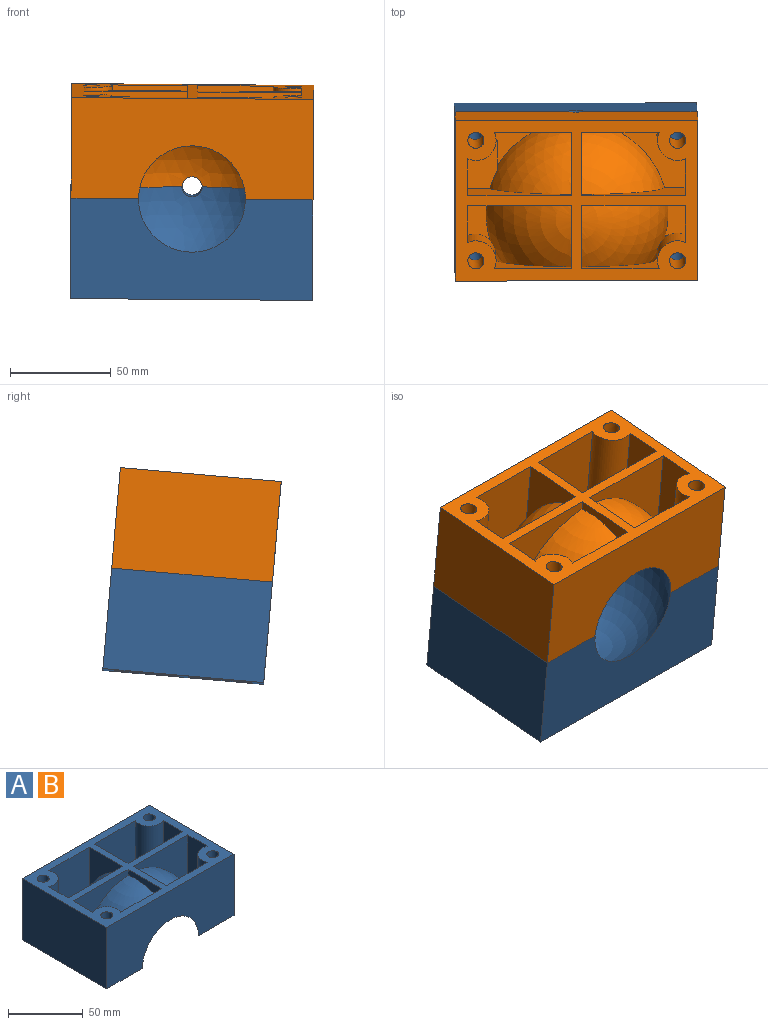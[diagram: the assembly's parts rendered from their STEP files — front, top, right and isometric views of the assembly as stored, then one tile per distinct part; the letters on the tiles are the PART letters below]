
ASSEMBLY  parts=2 mates=1
PART A: 56 faces, bbox 120x95.4x54 mm
  f0: sphere r=46mm, area 1832.9mm2, adj f1,f2,f8,f35,f38,f55
  f1: plane 44x38.34mm, normal (0,1,0), area 794.8mm2, adj f0,f17,f35,f38,f55
  f2: plane 51.5x39mm, normal (0,-1,0), area 971mm2, adj f0,f6,f8,f17,f55
  f3: plane 44x38.35mm, normal (0,-1,0), area 1642mm2, adj f4,f17,f37,f41,f53
  f4: sphere r=46mm, area 1825.4mm2, adj f3,f5,f34,f41,f49,f53
  f5: plane 51.5x39mm, normal (0,1,0), area 1034.3mm2, adj f4,f17,f34,f36,f53
  f6: plane 39x18.34mm, normal (1,0,0), area 715.1mm2, adj f2,f8,f17,f35
  f7: plane 44x18.34mm, normal (-1,0,0), area 806.7mm2, adj f9,f17,f46,f50
  f8: plane 20.7x11.33mm, normal (0,0,1), area 175.6mm2, adj f0,f2,f6,f35
  f9: plane 19.5x10mm, normal (0,0,1), area 156.5mm2, adj f7,f10,f46,f50
  f10: sphere r=46mm, area 1935.8mm2, adj f9,f40,f43,f46,f50,f54
  f11: plane 80x55mm, normal (0,0,-1), area 1917mm2, adj f13,f15,f16,f18,f19,f22,f23,f24
  f12: plane 80x55mm, normal (0,0,-1), area 1917mm2, adj f13,f14,f15,f18,f20,f21,f28,f29
  f13: plane 120x50mm, normal (0,1,0), area 5960.7mm2, adj f11,f12,f14,f16,f17,f33
  f14: plane 80x50mm, normal (-1,0,0), area 4000mm2, adj f12,f13,f15,f17
  f15: plane 120x50mm, normal (0,-1,0), area 4900.4mm2, adj f11,f12,f14,f16,f17,f18
  f16: plane 80x50mm, normal (1,0,0), area 4000mm2, adj f11,f13,f15,f17
  f17: plane 120x80mm, normal (0,0,1), area 3599.3mm2, adj f1,f2,f3,f5,f6,f7,f13,f14
  f18: sphere r=40mm, area 8757mm2, adj f11,f12,f15,f33
  f19: cylinder r=4mm len=50mm, axis (0,0,-1), area 1256.6mm2, adj f11,f17
  f20: cylinder r=4mm len=50mm, axis (0,0,-1), area 1256.6mm2, adj f12,f17
  f21: cylinder r=4mm len=50mm, axis (0,0,-1), area 1256.6mm2, adj f12,f17
  f22: cylinder r=4mm len=50mm, axis (0,0,-1), area 1256.6mm2, adj f11,f17
  f23: plane 10x4mm, normal (0,-1,0), area 40mm2, adj f11,f24,f26,f27
  f24: plane 40x4mm, normal (-1,0,0), area 160mm2, adj f11,f23,f25,f27
  f25: plane 10x4mm, normal (0,1,0), area 40mm2, adj f11,f24,f26,f27
  f26: plane 40x4mm, normal (1,0,0), area 160mm2, adj f11,f23,f25,f27
  f27: plane 40x10mm, normal (0,0,-1), area 400mm2, adj f23,f24,f25,f26
  f28: plane 10x5mm, normal (0,1,0), area 50mm2, adj f12,f29,f31,f32
  f29: plane 40x5mm, normal (1,0,0), area 200mm2, adj f12,f28,f30,f32
  f30: plane 10x5mm, normal (0,-1,0), area 50mm2, adj f12,f29,f31,f32
  f31: plane 40x5mm, normal (-1,0,0), area 200mm2, adj f12,f28,f30,f32
  f32: plane 40x10mm, normal (0,0,-1), area 400mm2, adj f28,f29,f30,f31
  f33: cylinder r=5mm len=10.31mm, axis (0,1,0), area 162mm2, adj f11,f12,f13,f18
  f34: plane 23.5x15mm, normal (0,0,1), area 270.1mm2, adj f4,f5,f36,f37,f48,f49
  f35: cylinder r=10mm len=44mm, axis (0,0,-1), area 935.1mm2, adj f0,f1,f6,f8,f17,f38
  f36: plane 39x18.33mm, normal (1,0,0), area 714.8mm2, adj f5,f17,f34,f37
  f37: cylinder r=10mm len=44mm, axis (0,0,-1), area 974.2mm2, adj f3,f17,f34,f36,f41,f48
  f38: plane 2.35x2.05mm, normal (0,0,1), area 2.2mm2, adj f0,f1,f35
  f39: plane 42x31.5mm, normal (0,0,1), area 470.6mm2, adj f42,f44,f45,f47,f51
  f40: plane 2.35x2.05mm, normal (0,0,1), area 2.2mm2, adj f10,f43,f46
  f41: plane 28.85x20.36mm, normal (0,0,1), area 211.3mm2, adj f3,f4,f37,f48,f49
  f42: plane 44x38.32mm, normal (0,-1,0), area 1640.9mm2, adj f17,f39,f45,f47,f52
  f43: plane 44x38.34mm, normal (0,1,0), area 794.8mm2, adj f10,f17,f40,f46,f54
  f44: plane 44x18.34mm, normal (-1,0,0), area 807mm2, adj f17,f39,f47,f51
  f45: sphere r=46mm, area 1882.6mm2, adj f39,f42,f51,f52
  f46: cylinder r=10mm len=44mm, axis (0,0,-1), area 991.7mm2, adj f7,f9,f10,f17,f40,f43
  f47: cylinder r=10mm len=44mm, axis (0,0,-1), area 1053.9mm2, adj f17,f39,f42,f44
  f48: plane 5x1.85mm, normal (0,1,0), area 9.2mm2, adj f34,f37,f41,f49
  f49: plane 14.23x5mm, normal (1,0,0), area 65.9mm2, adj f4,f34,f41,f48
  f50: plane 51.5x44mm, normal (0,-1,0), area 1018.2mm2, adj f7,f9,f10,f17,f54
  f51: plane 51.5x44mm, normal (0,1,0), area 1087.2mm2, adj f17,f39,f44,f45,f52
  f52: plane 36.82x31.5mm, normal (1,0,0), area 502mm2, adj f17,f42,f45,f51
  f53: plane 36.82x31.5mm, normal (-1,0,0), area 502mm2, adj f3,f4,f5,f17
  f54: plane 31.5x10.84mm, normal (1,0,0), area 182.1mm2, adj f10,f17,f43,f50
  f55: plane 31.5x10.84mm, normal (-1,0,0), area 182.1mm2, adj f0,f1,f2,f17
PART B: same geometry as A
PLACE A rot(axis=(0,-1,-0.04),179.6deg) t=(42.09,20.47,-15.14)mm
PLACE B rot(axis=(1,0.09,0),5deg) t=(42.09,20.47,-15.14)mm
MATE fastened B.f19 <-> A.f21  axis (-0.01,0.09,-1) through (92.08,0.56,-17.26)mm
